# Revit family: oventrop_flypass-4tz-set-1_1149550-51rfa
name_source: partatom
category: Арматура трубопроводов
revit_build: Autodesk Revit 2017 (Build: 20160225_1515(x64)
units: mm (PartAtom-declared; Revit-internal decimal feet)

## family parameters
Всегда вертикально = Да
Заголовок OmniClass = Adjusting/Controlling Valves for Liquid Services
На основе рабочей плоскости = Нет
Номер OmniClass = 23.65.55.14.17
Общий = Нет
При загрузке вырезать с полостями = Нет
Размер круглого соединителя = Использовать радиус
Тип детали = Нормальный

## types (2) — shared parameters
Black = Color RGB 035-035-035
Body Diameter = 19 мм
Connection Diameter 1 = 34 мм
Connection Distance 1 = 63.999 мм
Connection Length = 65 мм
Connection Piece Length = 5 мм
Connection Radius 2 = 17 мм
Custom = Нет
EMCS Version = 2.0
ETIM Article Class = EC011463
External Length 1 = 10.2 мм
Family Version = 10.16
Filter External Length = 12.3 мм
Handle Height = 10 мм
Handle Height 2 = 50 мм
Height 1 = 93 мм
Height 2 = 74 мм
IFCExportAs = IfcValveType
IFCExportType = PRESSUREREDUCING
Kv Value = 0.0 л/с
Length = 166 мм
MEPcontent Class = VALVE_BALANCING
Manufacturer URL = http://www.oventrop.com
Product Line = Oventrop
Reduced Body Diameter = 18 мм
Revit Version = 2015
Strainer Length = 70 мм
Use Nominal Diameter = Да
Yellow = Color RGB 168-128-048
Изготовитель = Oventrop
zero-valued in all types: Kvs Value

## per-type parameters (varying)
- DN 15: Article Description=OVENTROP-CONNECTION "Flypass Set 1", DN15, 1/2", Cocon QTZ, strainer; Connection Diameter 2=32 мм; Connection Distance 2=63.999 мм; Connection Radius 1=16 мм; DN 15=Да; DN 20=Нет; External Length=12.2 мм; External Length 2=10.2 мм; Filter Length=62.527 мм; GTIN=4026755408683; Increased Outer Radius=11.65 мм; Manufacturer Art. No.=1149550; Nominal Diameter 1=12.7 мм; Nominal Diameter 2=19 мм; Nominal Radius 1=9.5 мм; Nominal Radius 2=6.35 мм; Outer Diameter 1=21.3 мм; Outer Diameter 2=26.9 мм; Outer Radius=13.45 мм; Outer Radius 1=13.45 мм; Outer Radius 2=10.65 мм; Reduced Connection Diameter=14 мм; URL=www.stabiplan.com; Width=82.649 мм; Описание=OVENTROP-CONNECTION "Flypass Set 1", DN15, 1/2", Cocon QTZ, strainer
- DN 20: Article Description=OVENTROP-CONNECTION "Flypass Set 1", DN20, 3/4", Cocon QTZ, strainer; Connection Diameter 2=38 мм; Connection Distance 2=65.471 мм; Connection Radius 1=19 мм; DN 15=Нет; DN 20=Да; External Length=15.2 мм; External Length 2=10 мм; Filter Length=63.999 мм; GTIN=4026755408690; Increased Outer Radius=14.45 мм; Manufacturer Art. No.=1149551; Nominal Diameter 1=19 мм; Nominal Diameter 2=25.4 мм; Nominal Radius 1=12.7 мм; Nominal Radius 2=9.5 мм; Outer Diameter 1=26.9 мм; Outer Diameter 2=33.7 мм; Outer Radius=17 мм; Outer Radius 1=16.85 мм; Outer Radius 2=13.45 мм; Reduced Connection Diameter=17 мм; URL=http://file-system.ru; Width=74 мм; Описание=OVENTROP-CONNECTION "Flypass Set 1", DN20, 3/4", Cocon QTZ, strainer

note: column(s) folded — value = type name in every type: Article Type, Группа модели

## geometry (parser evidence)
native form markers: Blend x12, Sweep x12
no freeform markers — native parametric forms only
